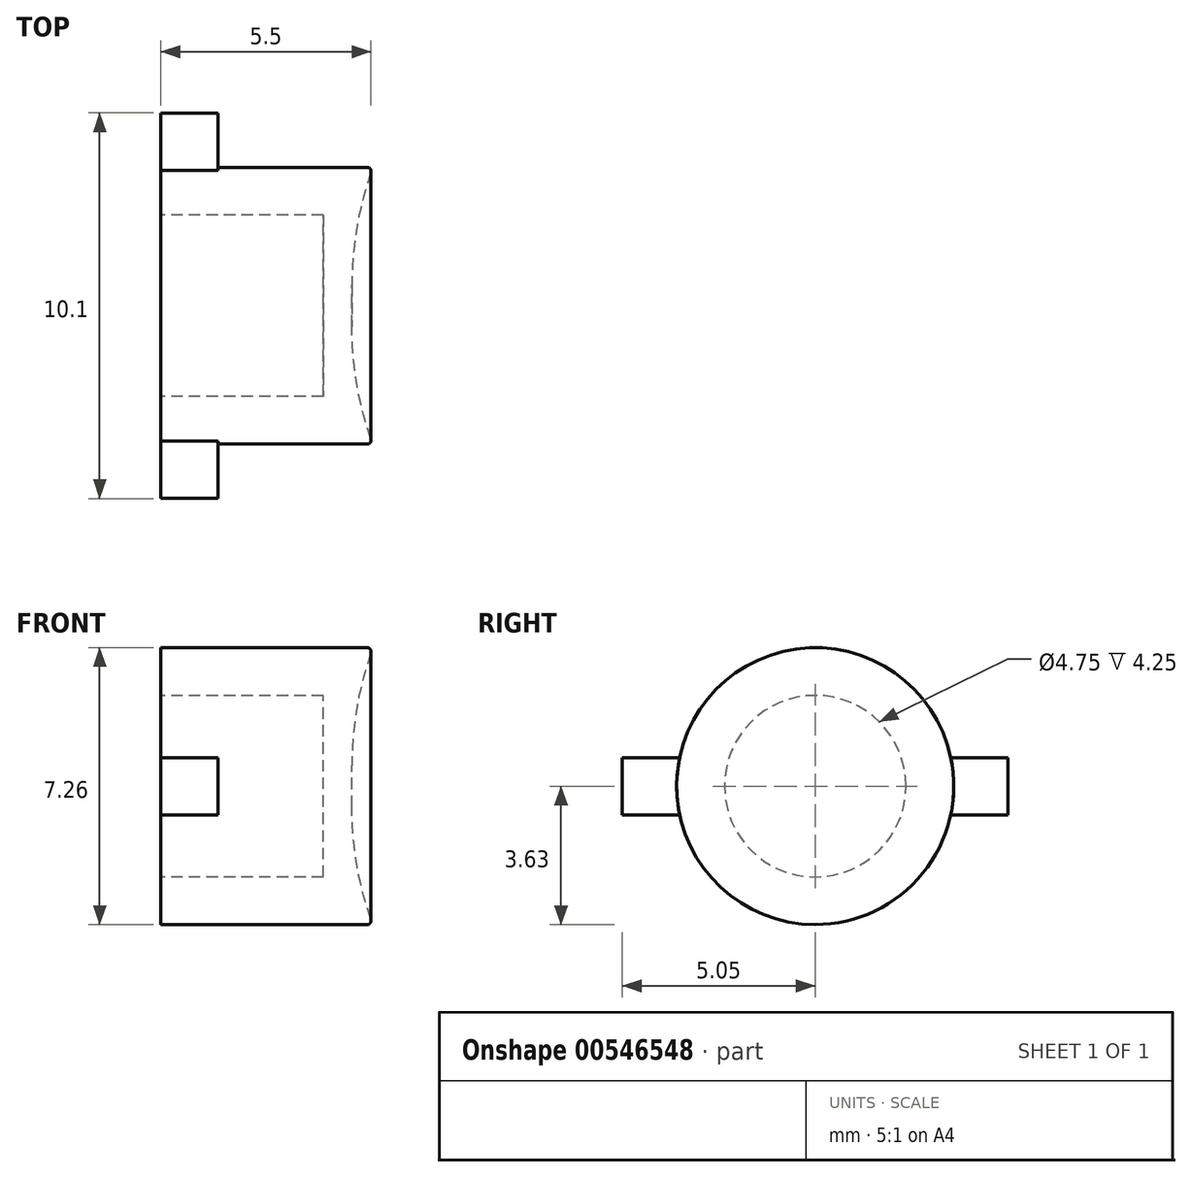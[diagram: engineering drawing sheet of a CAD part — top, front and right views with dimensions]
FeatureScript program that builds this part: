
annotation { "Feature Type Name" : "Feature", "Feature Type Description" : "" }
export const myFeature = defineFeature(function(context is Context, id is Id, definition is map)
    precondition{}
    {
        {
            var Q0;
            Q0=qCreatedBy(makeId("Right.planeOp"),FACE);
            var sketch = newSketch(context, id + "F0", { "sketchPlane" : qUnion([Q0])});
            skCircle(sketch, "E0", {"center": v(0, 0) * mm, "radius": 3.62 * mm});
            skSolve(sketch);
        }
        {
            var Q0;
            Q0=makeQuery(id+"F0.imprint","IMPRINT",FACE,{"disambiguationData":[TD([[makeQuery(id+"F0.imprint","IMPRINT",EDGE,{"derivedFrom":sQuery(id+"F0.wireOp",EDGE,"E0")}),1.0]])]});
            extrude(context, id + "F1", {"entities" : qUnion([Q0]), "endBound" : BoundingType.SYMMETRIC, "depth" : 5.5 * mm, "offsetDistance" : 25 * mm});
        }
        {
            var Q0;
            Q0=makeQuery(id+"F1.opExtrude","CAP_FACE",FACE,{"disambiguationData":[OSD([sQuery(id+"F0.wireOp",EDGE,"E0")])],"isStart":true});
            shell(context, id + "F2", {"entities" : qUnion([Q0]), "thickness" : 1.25 * mm});
        }
        {
            var Q0;
            Q0=makeQuery(id+"F1.opExtrude","CAP_FACE",FACE,{"disambiguationData":[OSD([sQuery(id+"F0.wireOp",EDGE,"E0")])],"isStart":true});
            var sketch = newSketch(context, id + "F3", { "sketchPlane" : qUnion([Q0])});
            skLineSegment(sketch, "E1.left", {"start": v(5.05, -0.75) * mm, "end": v(5.05, 0.75) * mm});
            skLineSegment(sketch, "E2.left", {"start": v(-5.05, 0.75) * mm, "end": v(-5.05, -0.75) * mm});
            skLineSegment(sketch, "E3", {"start": v(5.05, 0.75) * mm, "end": v(3.55, 0.75) * mm});
            skLineSegment(sketch, "E4", {"start": v(5.05, -0.75) * mm, "end": v(3.55, -0.75) * mm});
            skArc(sketch, "E5", {"start": v(-3.55, 0.75) * mm, "mid": v(-3.63, 0) * mm, "end": v(-3.55, -0.75) * mm});
            skLineSegment(sketch, "E6", {"start": v(-5.05, 0.75) * mm, "end": v(-3.55, 0.75) * mm});
            skLineSegment(sketch, "E7", {"start": v(-5.05, -0.75) * mm, "end": v(-3.55, -0.75) * mm});
            skArc(sketch, "E8.trimOffspring", {"start": v(3.55, -0.75) * mm, "mid": v(3.63, 0) * mm, "end": v(3.55, 0.75) * mm});
            skPoint(sketch, "E9", {"position": v(5.05, 0) * mm});
            skPoint(sketch, "E10", {"position": v(-5.05, 0) * mm});
            skSolve(sketch);
        }
        {
            var Q0;
            Q0=qSketchRegion(id+"F3",true);
            extrude(context, id + "F4", {"entities" : qUnion([Q0]), "operationType" : NewBodyOperationType.ADD, "oppositeDirection" : true, "depth" : 1.5 * mm, "offsetDistance" : 25 * mm});
        }
        {
            var Q0;
            Q0=makeQuery(id+"F1.opExtrude","CAP_FACE",FACE,{"disambiguationData":[OSD([sQuery(id+"F0.wireOp",EDGE,"E0")])],"isStart":false});
            var sketch = newSketch(context, id + "F5", { "sketchPlane" : qUnion([Q0])});
            skCircle(sketch, "E11", {"center": v(0, 0) * mm, "radius": 3.5 * mm});
            skSolve(sketch);
        }
        {
            var Q0;
            Q0=qSketchRegion(id+"F5",true);
            extrude(context, id + "F6", {"entities" : qUnion([Q0]), "operationType" : NewBodyOperationType.REMOVE, "oppositeDirection" : true, "depth" : .5 * mm, "offsetDistance" : 25 * mm});
        }
        {
            var Q0;
            Q0=makeQuery(id+"F6.boolean.opBoolean","COPY",FACE,{"derivedFrom":makeQuery(id+"F6.opExtrude","CAP_FACE",FACE,{"disambiguationData":[OSD([sQuery(id+"F5.wireOp",EDGE,"E11")])],"isStart":false})});
            fillet(context, id + "F7", {"entities" : qUnion([Q0]), "radius" : 9 * mm, "tangentPropagation" : true, "allowEdgeOverflow" : false});
        }
        {
            var Q0;
            Q0=makeQuery(id+"F7.opFillet","BLEND_EDGE",EDGE,{"blendedFrom":[makeQuery(id+"F6.boolean.opBoolean","COPY",EDGE,{"derivedFrom":makeQuery(id+"F6.opExtrude","CAP_EDGE",EDGE,{"disambiguationData":[OSD([sQuery(id+"F5.wireOp",EDGE,"E11")])],"isStart":false})}),makeQuery(id+"F1.opExtrude","CAP_FACE",FACE,{"disambiguationData":[OSD([sQuery(id+"F0.wireOp",EDGE,"E0")])],"isStart":false})],"blendedInto":[makeQuery(id+"F1.opExtrude","CAP_FACE",FACE,{"disambiguationData":[OSD([sQuery(id+"F0.wireOp",EDGE,"E0")])],"isStart":false})]});
            var Q1;
            Q1=makeQuery(id+"F1.opExtrude","CAP_EDGE",EDGE,{"disambiguationData":[OSD([sQuery(id+"F0.wireOp",EDGE,"E0")])],"isStart":false});
            fillet(context, id + "F8", {"entities" : qUnion([Q0, Q1]), "radius" : .1 * mm, "tangentPropagation" : true, "allowEdgeOverflow" : false});
        }
    });
